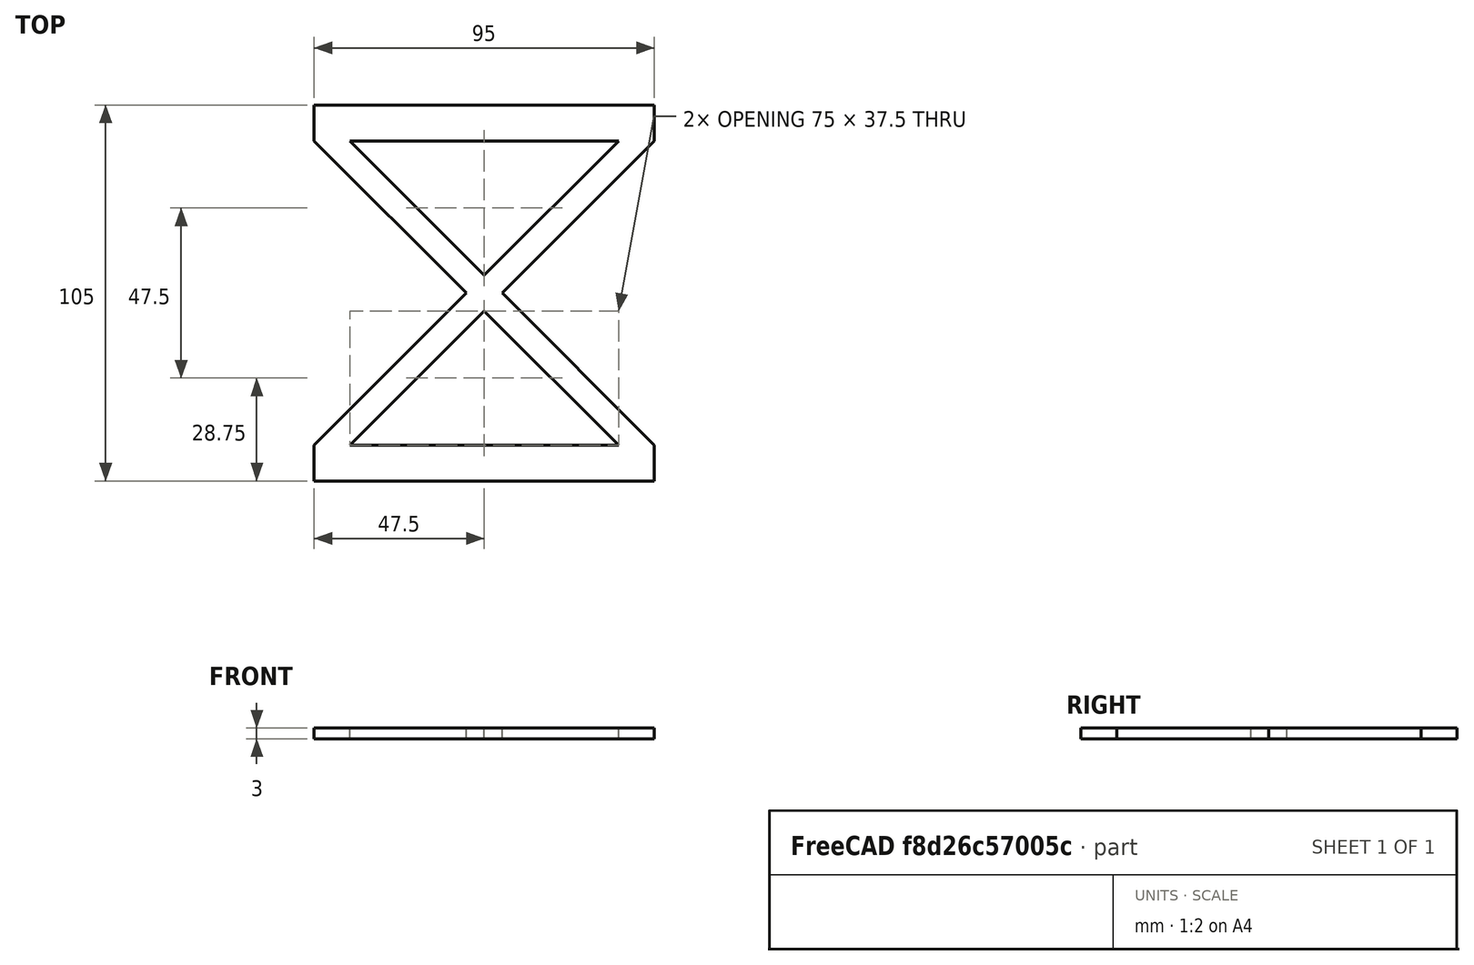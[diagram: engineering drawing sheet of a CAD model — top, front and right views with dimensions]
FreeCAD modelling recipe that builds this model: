
FCSTD DOCUMENT  (FreeCAD 1.0R39109 (Git))
Label: KabelkanalKreuz
License: All rights reserved
LicenseURL: https://en.wikipedia.org/wiki/All_rights_reserved
objects: Sketcher::SketchObject×1, PartDesign::Pad×1, PartDesign::Body×1
note: 6 computed .brp shape members not serialized (recipe doc carries the construction recipe); baked Part::Feature solids carry a one-line shape summary decoded from their .brp

FEATURE [Sketcher::SketchObject] Sketch
  ArcFitTolerance = 1e-06
  AttachmentSupport = -> [XY_Plane]
  FullyConstrained = true
  MakeInternals = false
  MapMode = 5
  sketch-geometry (22):
    g0: LineSegment StartX=0 StartY=0 StartZ=0 EndX=95 EndY=0 EndZ=0
    g1: LineSegment StartX=95 StartY=0 StartZ=0 EndX=95 EndY=10 EndZ=0
    g2: LineSegment StartX=0 StartY=105 StartZ=0 EndX=95 EndY=105 EndZ=0
    g3: LineSegment StartX=95 StartY=105 StartZ=0 EndX=95 EndY=95 EndZ=0
    g4: LineSegment StartX=0 StartY=0 StartZ=0 EndX=0 EndY=10 EndZ=0
    g5: LineSegment StartX=85 StartY=95 StartZ=0 EndX=10 EndY=95 EndZ=0
    g6: LineSegment StartX=0 StartY=105 StartZ=0 EndX=0 EndY=95 EndZ=0
    g7: LineSegment StartX=10 StartY=95 StartZ=0 EndX=47.5 EndY=57.5 EndZ=0
    g8: LineSegment StartX=47.5 StartY=57.5 StartZ=0 EndX=85 EndY=95 EndZ=0
    g9: LineSegment StartX=0 StartY=95 StartZ=0 EndX=42.5 EndY=52.5 EndZ=0
    g10: LineSegment StartX=42.5 StartY=52.5 StartZ=0 EndX=0 EndY=10 EndZ=0
    g11: LineSegment StartX=95 StartY=95 StartZ=0 EndX=52.5 EndY=52.5 EndZ=0
    g12: LineSegment StartX=52.5 StartY=52.5 StartZ=0 EndX=95 EndY=10 EndZ=0
    g13: LineSegment StartX=10 StartY=10 StartZ=0 EndX=85 EndY=10 EndZ=0
    g14: LineSegment StartX=85 StartY=10 StartZ=0 EndX=47.5 EndY=47.5 EndZ=0
    g15: LineSegment StartX=47.5 StartY=47.5 StartZ=0 EndX=10 EndY=10 EndZ=0
    g16: LineSegment [constr] StartX=0 StartY=10 StartZ=0 EndX=10 EndY=10 EndZ=0
    g17: LineSegment [constr] StartX=85 StartY=10 StartZ=0 EndX=95 EndY=10 EndZ=0
    g18: LineSegment [constr] StartX=0 StartY=95 StartZ=0 EndX=10 EndY=95 EndZ=0
    g19: LineSegment [constr] StartX=85 StartY=95 StartZ=0 EndX=95 EndY=95 EndZ=0
    g20: LineSegment [constr] StartX=47.5 StartY=57.5 StartZ=0 EndX=47.5 EndY=47.5 EndZ=0
    g21: LineSegment [constr] StartX=42.5 StartY=52.5 StartZ=0 EndX=52.5 EndY=52.5 EndZ=0
  constraints (59):
    c: Coincident(g0,g-1)
    c: PointOnObject(g0,g-1)
    c: Coincident(g1,g0)
    c: Vertical(g1)
    c: Horizontal(g2)
    c: Vertical(g3)
    c: Coincident(g4,g0)
    c: PointOnObject(g4,g-2)
    c: Horizontal(g5)
    c: Coincident(g3,g2)
    c: Coincident(g6,g2)
    c: PointOnObject(g6,g-2)
    c: Vertical(g6)
    c: Coincident(g7,g5)
    c: Coincident(g8,g7)
    c: Coincident(g8,g5)
    c: Coincident(g9,g6)
    c: Coincident(g10,g9)
    c: Coincident(g10,g4)
    c: Coincident(g11,g3)
    c: Coincident(g12,g11)
    c: Coincident(g12,g1)
    c: Horizontal(g13)
    c: Coincident(g14,g13)
    c: Coincident(g15,g14)
    c: Coincident(g15,g13)
    c: Equal(g10,g9)
    c: Equal(g11,g12)
    c: Equal(g12,g10)
    c: Equal(g3,g6)
    c: Equal(g6,g4)
    c: Equal(g4,g1)
    c: Equal(g15,g14)
    c: Equal(g14,g8)
    c: Equal(g8,g7)
    c: Equal(g5,g13)
    c: Equal(g0,g2)
    c: DistanceX(g0,g0) = 95
    c: DistanceY(g1,g1) = 10
    c: Angle(g0,g10) = 0.785398
    c: Coincident(g16,g4)
    c: Coincident(g16,g13)
    c: Horizontal(g16)
    c: Coincident(g17,g13)
    c: Coincident(g17,g1)
    c: Equal(g17,g16)
    c: DistanceX(g16,g16) = 10
    c: Coincident(g18,g6)
    c: Coincident(g18,g5)
    c: Coincident(g19,g5)
    c: Coincident(g19,g3)
    c: Horizontal(g18)
    c: Angle(g14,g13) = 0.785398
    c: Coincident(g20,g7)
    c: Coincident(g20,g14)
    c: Coincident(g21,g9)
    c: Coincident(g21,g11)
    c: Vertical(g20)
    c: Equal(g20,g21)
FEATURE [PartDesign::Pad] Pad
  Direction = (0,0,1)
  Length = 3
  Length2 = 10
  Profile = -> Sketch
  ReferenceAxis = -> Sketch [N_Axis]
  Refine = true
  Suppressed = false
  Type = 0
FEATURE [PartDesign::Body] Body  label="Körper"
  AllowCompound = false
  Group = -> [Sketch,Pad]
  Origin = -> Origin
  Tip = -> Pad
